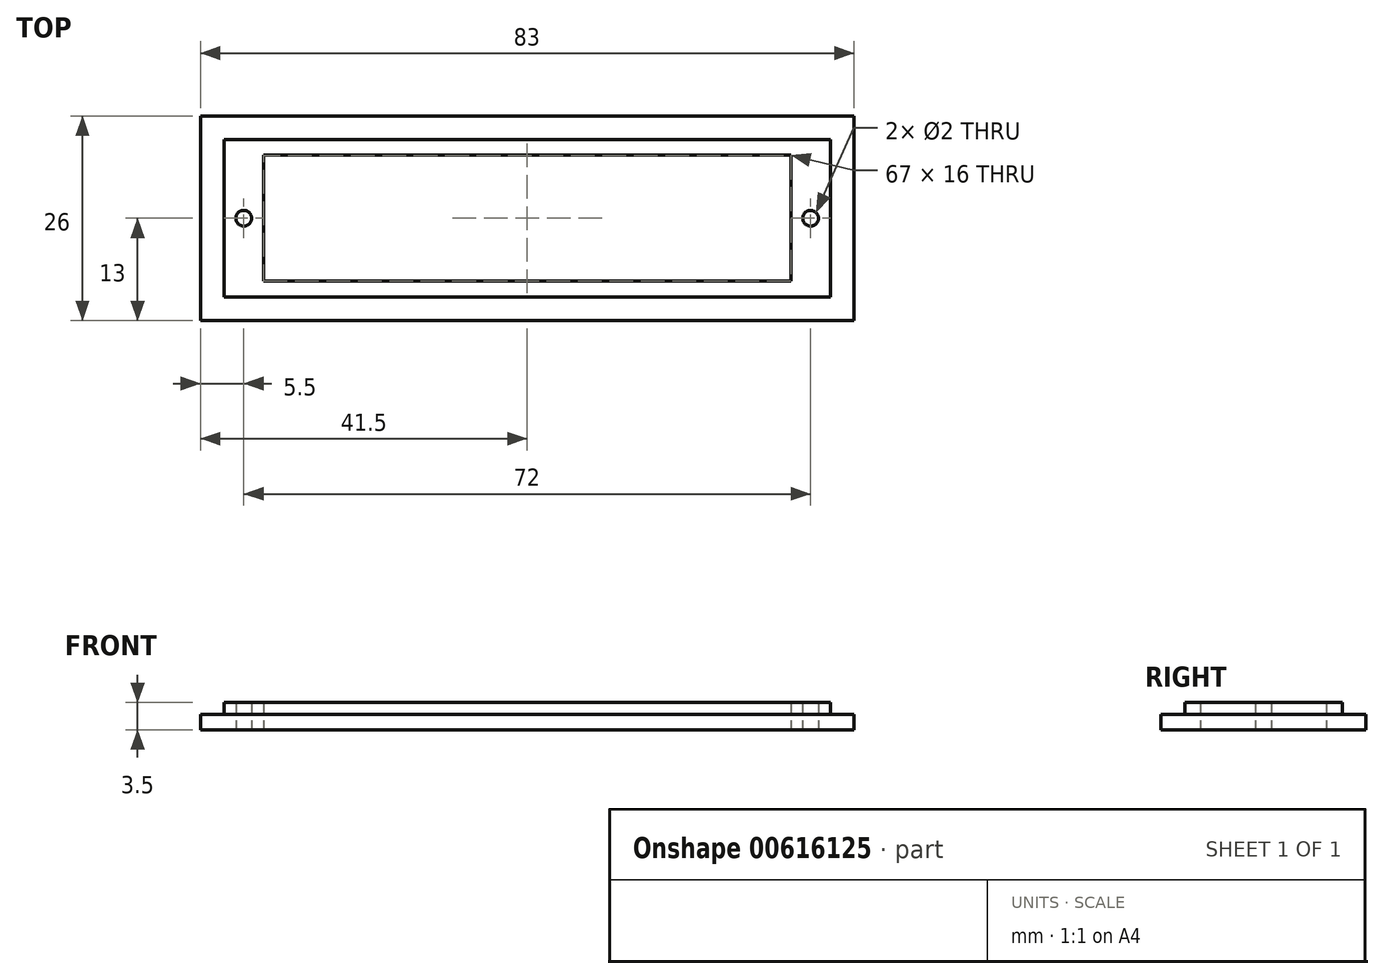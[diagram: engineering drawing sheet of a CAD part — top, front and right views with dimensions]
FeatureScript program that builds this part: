
annotation { "Feature Type Name" : "Feature", "Feature Type Description" : "" }
export const myFeature = defineFeature(function(context is Context, id is Id, definition is map)
    precondition{}
    {
        {
            var Q0;
            Q0=qCreatedBy(makeId("Top.planeOp"),FACE);
            var sketch = newSketch(context, id + "F0", { "sketchPlane" : qUnion([Q0])});
            skLineSegment(sketch, "E0.bottom", {"start": v(41.5, 13) * mm, "end": v(-41.5, 13) * mm});
            skLineSegment(sketch, "E0.top", {"start": v(41.5, -13) * mm, "end": v(-41.5, -13) * mm});
            skLineSegment(sketch, "E0.left", {"start": v(41.5, 13) * mm, "end": v(41.5, -13) * mm});
            skLineSegment(sketch, "E0.right", {"start": v(-41.5, 13) * mm, "end": v(-41.5, -13) * mm});
            skPoint(sketch, "E0.middle", {"position": v(0, 0) * mm});
            skLineSegment(sketch, "E1.bottom", {"start": v(33.5, 8) * mm, "end": v(-33.5, 8) * mm});
            skLineSegment(sketch, "E1.top", {"start": v(33.5, -8) * mm, "end": v(-33.5, -8) * mm});
            skLineSegment(sketch, "E1.left", {"start": v(33.5, 8) * mm, "end": v(33.5, -8) * mm});
            skLineSegment(sketch, "E1.right", {"start": v(-33.5, 8) * mm, "end": v(-33.5, -8) * mm});
            skSolve(sketch);
        }
        {
            var Q0;
            Q0 = qSketchRegion(id + "F0", true);
            extrude(context, id + "F1", {"entities" : qUnion([Q0]), "depth" : 2 * mm, "offsetDistance" : 25 * mm});
        }
        {
            var Q0;
            Q0=makeQuery(id+"F1.opExtrude","CAP_FACE",FACE,{"disambiguationData":[OSD([sQuery(id+"F0.wireOp",EDGE,"E0.bottom"),sQuery(id+"F0.wireOp",EDGE,"E0.top"),sQuery(id+"F0.wireOp",EDGE,"E0.left"),sQuery(id+"F0.wireOp",EDGE,"E0.right"),sQuery(id+"F0.wireOp",EDGE,"E1.bottom"),sQuery(id+"F0.wireOp",EDGE,"E1.top"),sQuery(id+"F0.wireOp",EDGE,"E1.left"),sQuery(id+"F0.wireOp",EDGE,"E1.right")])],"isStart":false});
            var sketch = newSketch(context, id + "F2", { "sketchPlane" : qUnion([Q0])});
            skLineSegment(sketch, "E2.bottom", {"start": v(-33.5, -8) * mm, "end": v(33.5, -8) * mm});
            skLineSegment(sketch, "E2.top", {"start": v(-33.5, 8) * mm, "end": v(33.5, 8) * mm});
            skLineSegment(sketch, "E2.left", {"start": v(-33.5, -8) * mm, "end": v(-33.5, 8) * mm});
            skLineSegment(sketch, "E2.right", {"start": v(33.5, -8) * mm, "end": v(33.5, 8) * mm});
            skLineSegment(sketch, "E3.bottom", {"start": v(38.5, 10) * mm, "end": v(-38.5, 10) * mm});
            skLineSegment(sketch, "E3.top", {"start": v(38.5, -10) * mm, "end": v(-38.5, -10) * mm});
            skLineSegment(sketch, "E3.left", {"start": v(38.5, 10) * mm, "end": v(38.5, -10) * mm});
            skLineSegment(sketch, "E3.right", {"start": v(-38.5, 10) * mm, "end": v(-38.5, -10) * mm});
            skPoint(sketch, "E3.middle", {"position": v(0, 0) * mm});
            skSolve(sketch);
        }
        {
            var Q0;
            Q0 = qSketchRegion(id + "F2", true);
            extrude(context, id + "F3", {"entities" : qUnion([Q0]), "operationType" : NewBodyOperationType.ADD, "depth" : 1.5 * mm, "offsetDistance" : 25 * mm});
        }
        {
            var Q0;
            Q0=makeQuery(id+"F1.opExtrude","CAP_FACE",FACE,{"disambiguationData":[OSD([sQuery(id+"F0.wireOp",EDGE,"E0.bottom"),sQuery(id+"F0.wireOp",EDGE,"E0.top"),sQuery(id+"F0.wireOp",EDGE,"E0.left"),sQuery(id+"F0.wireOp",EDGE,"E0.right"),sQuery(id+"F0.wireOp",EDGE,"E1.bottom"),sQuery(id+"F0.wireOp",EDGE,"E1.top"),sQuery(id+"F0.wireOp",EDGE,"E1.left"),sQuery(id+"F0.wireOp",EDGE,"E1.right")])],"isStart":true});
            var sketch = newSketch(context, id + "F4", { "sketchPlane" : qUnion([Q0])});
            skPoint(sketch, "E4", {"position": v(-36, 0) * mm});
            skPoint(sketch, "E5", {"position": v(36, 0) * mm});
            skPoint(sketch, "E5.positionSnap0", {"position": v(-33.5, 0) * mm});
            skCircle(sketch, "E6", {"center": v(-36, 0) * mm, "radius": 1 * mm});
            skCircle(sketch, "E7", {"center": v(36, 0) * mm, "radius": 1 * mm});
            skSolve(sketch);
        }
        {
            var Q0;
            Q0 = qSketchRegion(id + "F4", true);
            extrude(context, id + "F5", {"entities" : qUnion([Q0]), "operationType" : NewBodyOperationType.REMOVE, "oppositeDirection" : true, "depth" : 25 * mm, "offsetDistance" : 25 * mm});
        }
        {
            var Q0;
            Q0=makeQuery(id+"F1.opExtrude","CAP_FACE",FACE,{"disambiguationData":[OSD([sQuery(id+"F0.wireOp",EDGE,"E0.bottom"),sQuery(id+"F0.wireOp",EDGE,"E0.top"),sQuery(id+"F0.wireOp",EDGE,"E0.left"),sQuery(id+"F0.wireOp",EDGE,"E0.right"),sQuery(id+"F0.wireOp",EDGE,"E1.bottom"),sQuery(id+"F0.wireOp",EDGE,"E1.top"),sQuery(id+"F0.wireOp",EDGE,"E1.left"),sQuery(id+"F0.wireOp",EDGE,"E1.right")])],"isStart":true});
            var sketch = newSketch(context, id + "F6", { "sketchPlane" : qUnion([Q0])});
            skCircle(sketch, "E8", {"center": v(-36, 0) * mm, "radius": 3 * mm});
            skCircle(sketch, "E9", {"center": v(36, 0) * mm, "radius": 3 * mm});
            skSolve(sketch);
        }
        {
            var Q0;
            Q0=makeQuery(id+"F6.imprint","IMPRINT",FACE,{"disambiguationData":[TD([[makeQuery(id+"F6.imprint","IMPRINT",EDGE,{"derivedFrom":makeQuery(id+"F5.boolean.opBoolean","COPY",EDGE,{"derivedFrom":makeQuery(id+"F5.opExtrude","CAP_EDGE",EDGE,{"disambiguationData":[OSD([sQuery(id+"F4.wireOp",EDGE,"E6")])],"isStart":true})})}),1.0]])]});
            var Q1;
            Q1=makeQuery(id+"F6.imprint","IMPRINT",FACE,{"disambiguationData":[TD([[makeQuery(id+"F6.imprint","IMPRINT",EDGE,{"derivedFrom":makeQuery(id+"F5.boolean.opBoolean","COPY",EDGE,{"derivedFrom":makeQuery(id+"F5.opExtrude","CAP_EDGE",EDGE,{"disambiguationData":[OSD([sQuery(id+"F4.wireOp",EDGE,"E7")])],"isStart":true})})}),1.0]])]});
            var Q2;
            {var subQ0=sQuery(id+"F6.wireOp",EDGE,"E8");var subQ1=makeQuery(id+"F1.opExtrude","CAP_EDGE",EDGE,{"disambiguationData":[OSD([sQuery(id+"F0.wireOp",EDGE,"E1.right")])],"isStart":true});var subQ2=makeQuery(id+"F6.imprint","INTERSECT",VERTEX,{"disambiguationData":[OD(0.0)],"derivedFrom":[subQ1,subQ0]});Q2=makeQuery(id+"F6.imprint","IMPRINT",FACE,{"disambiguationData":[TD([[makeQuery(id+"F6.imprint","IMPRINT",EDGE,{"disambiguationData":[TD([[subQ2,-1.0]])],"derivedFrom":subQ0}),1.0]])]});}
            var Q3;
            {var subQ0=sQuery(id+"F6.wireOp",EDGE,"E9");var subQ1=makeQuery(id+"F1.opExtrude","CAP_EDGE",EDGE,{"disambiguationData":[OSD([sQuery(id+"F0.wireOp",EDGE,"E1.left")])],"isStart":true});var subQ2=makeQuery(id+"F6.imprint","INTERSECT",VERTEX,{"disambiguationData":[OD(0.0)],"derivedFrom":[subQ1,subQ0]});Q3=makeQuery(id+"F6.imprint","IMPRINT",FACE,{"disambiguationData":[TD([[makeQuery(id+"F6.imprint","IMPRINT",EDGE,{"disambiguationData":[TD([[subQ2,1.0]])],"derivedFrom":subQ0}),1.0]])]});}
            var Q4;
            Q4=makeQuery(id+"F6.imprint","IMPRINT",FACE,{"disambiguationData":[TD([[makeQuery(id+"F6.imprint","IMPRINT",EDGE,{"derivedFrom":makeQuery(id+"F5.boolean.opBoolean","COPY",EDGE,{"derivedFrom":makeQuery(id+"F5.opExtrude","CAP_EDGE",EDGE,{"disambiguationData":[OSD([sQuery(id+"F4.wireOp",EDGE,"E7")])],"isStart":true})})}),-1.0]])]});
            var Q5;
            Q5=makeQuery(id+"F6.imprint","IMPRINT",FACE,{"disambiguationData":[TD([[makeQuery(id+"F6.imprint","IMPRINT",EDGE,{"derivedFrom":makeQuery(id+"F5.boolean.opBoolean","COPY",EDGE,{"derivedFrom":makeQuery(id+"F5.opExtrude","CAP_EDGE",EDGE,{"disambiguationData":[OSD([sQuery(id+"F4.wireOp",EDGE,"E6")])],"isStart":true})})}),-1.0]])]});
            extrude(context, id + "F7", {"entities" : qUnion([Q0, Q1, Q2, Q3, Q4, Q5]), "operationType" : NewBodyOperationType.REMOVE, "oppositeDirection" : true, "depth" : 2 * mm, "offsetDistance" : 25 * mm});
        }
    });
